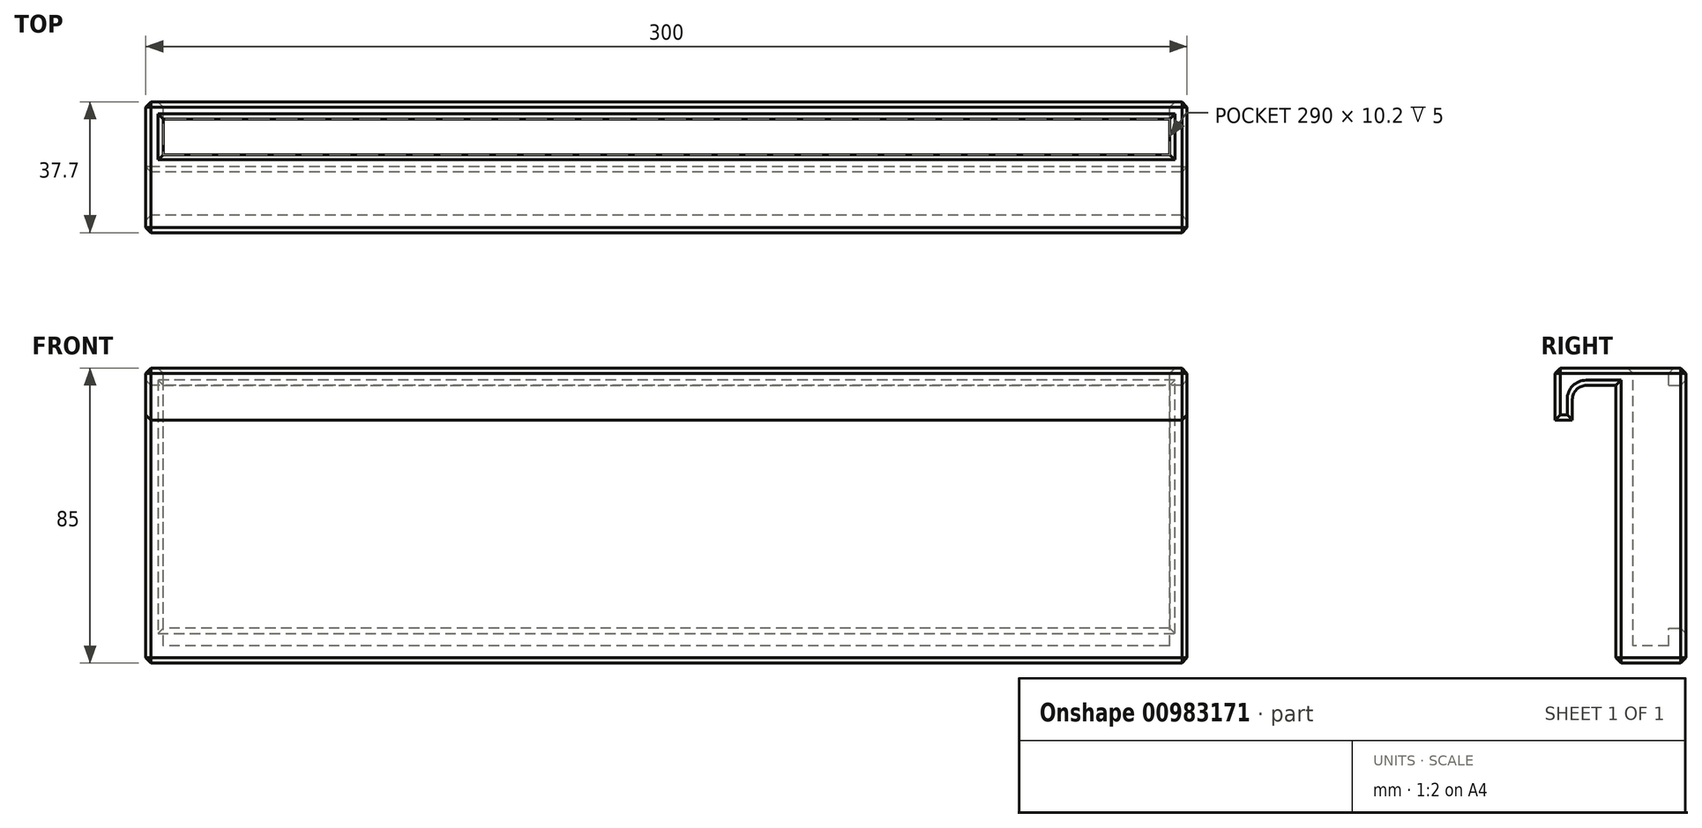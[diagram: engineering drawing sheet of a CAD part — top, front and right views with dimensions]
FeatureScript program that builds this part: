
annotation { "Feature Type Name" : "Feature", "Feature Type Description" : "" }
export const myFeature = defineFeature(function(context is Context, id is Id, definition is map)
    precondition{}
    {
        {
            var Q0;
            Q0=qCreatedBy(makeId("Right.planeOp"),FACE);
            var sketch = newSketch(context, id + "F0", { "sketchPlane" : qUnion([Q0])});
            skLineSegment(sketch, "E0.left", {"start": v(10.1, -42.5) * mm, "end": v(10.1, 42.5) * mm});
            skPoint(sketch, "E0.middle", {"position": v(0, 0) * mm});
            skLineSegment(sketch, "E1.top", {"start": v(5.1, -37.5) * mm, "end": v(-5.1, -37.5) * mm});
            skLineSegment(sketch, "E2.top", {"start": v(-10.1, 37.5) * mm, "end": v(-22.6, 37.5) * mm});
            skLineSegment(sketch, "E3.top", {"start": v(-22.6, 27.5) * mm, "end": v(-27.6, 27.5) * mm});
            skLineSegment(sketch, "E3.right", {"start": v(-27.6, 42.5) * mm, "end": v(-27.6, 27.5) * mm});
            skLineSegment(sketch, "E4.top", {"start": v(-5.1, 37.5) * mm, "end": v(5.1, 37.5) * mm});
            skLineSegment(sketch, "E5", {"start": v(5.1, -37.5) * mm, "end": v(5.1, 37.5) * mm});
            skLineSegment(sketch, "E6", {"start": v(-5.1, 37.5) * mm, "end": v(-5.1, -37.5) * mm});
            skLineSegment(sketch, "E7", {"start": v(-22.6, 37.5) * mm, "end": v(-22.6, 27.5) * mm});
            skLineSegment(sketch, "E8", {"start": v(-10.1, 37.5) * mm, "end": v(-10.1, -42.5) * mm});
            skLineSegment(sketch, "E9", {"start": v(-10.1, -42.5) * mm, "end": v(10.1, -42.5) * mm});
            skLineSegment(sketch, "E10", {"start": v(-27.6, 42.5) * mm, "end": v(10.1, 42.5) * mm});
            skLineSegment(sketch, "E11", {"start": v(0, 37.5) * mm, "end": v(0, -37.5) * mm, "construction": true});
            skLineSegment(sketch, "E12", {"start": v(-5.1, 0) * mm, "end": v(5.1, 0) * mm, "construction": true});
            skLineSegment(sketch, "E13", {"start": v(-16.35, 37.5) * mm, "end": v(-16.35, 20.18) * mm, "construction": true});
            skLineSegment(sketch, "E14", {"start": v(-22.6, 33.5) * mm, "end": v(-10.1, 33.5) * mm, "construction": true});
            skLineSegment(sketch, "E15", {"start": v(-18.6, 37.5) * mm, "end": v(-18.6, 19.62) * mm, "construction": true});
            skArc(sketch, "E16", {"start": v(-18.6, 37.5) * mm, "mid": v(-21.43, 36.33) * mm, "end": v(-22.6, 33.5) * mm});
            skLineSegment(sketch, "E17", {"start": v(-15.1, 37.5) * mm, "end": v(-15.1, 22.05) * mm, "construction": true});
            skLineSegment(sketch, "E18", {"start": v(-22.6, 32.5) * mm, "end": v(-10.1, 32.5) * mm, "construction": true});
            skArc(sketch, "E19", {"start": v(-15.1, 37.5) * mm, "mid": v(-11.56, 36.04) * mm, "end": v(-10.1, 32.5) * mm});
            skSolve(sketch);
        }
        {
            var Q0;
            Q0=makeQuery(id+"F0.imprint","IMPRINT",FACE,{"disambiguationData":[TD([[makeQuery(id+"F0.imprint","IMPRINT",EDGE,{"derivedFrom":sQuery(id+"F0.wireOp",EDGE,"E0.left")}),1.0]])]});
            var Q1;
            {var subQ3=sQuery(id+"F0.wireOp",EDGE,"7e27f287-87ae-4c6c-8f3d-3b3ba59f38b20.MirrorCS");Q1=makeQuery(id+"F0.imprint","IMPRINT",FACE,{"disambiguationData":[TD([[makeQuery(id+"F0.imprint","IMPRINT",EDGE,{"derivedFrom":subQ3}),1.0]])]});}
            var Q2;
            {var subQ3=sQuery(id+"F0.wireOp",EDGE,"E16");Q2=makeQuery(id+"F0.imprint","IMPRINT",FACE,{"disambiguationData":[TD([[makeQuery(id+"F0.imprint","IMPRINT",EDGE,{"derivedFrom":subQ3}),-1.0]])]});}
            var Q3;
            {var subQ3=sQuery(id+"F0.wireOp",EDGE,"E19");Q3=makeQuery(id+"F0.imprint","IMPRINT",FACE,{"disambiguationData":[TD([[makeQuery(id+"F0.imprint","IMPRINT",EDGE,{"derivedFrom":subQ3}),1.0]])]});}
            var Q4;
            Q4=makeQuery(id+"F0.imprint","IMPRINT",FACE,{"disambiguationData":[TD([[makeQuery(id+"F0.imprint","IMPRINT",EDGE,{"derivedFrom":sQuery(id+"F0.wireOp",EDGE,"E1.top")}),-1.0]])]});
            extrude(context, id + "F1", {"entities" : qUnion([Q0, Q1, Q2, Q3, Q4]), "depth" : 300 * mm, "offsetDistance" : 25 * mm});
        }
        {
            var Q0;
            Q0=makeQuery(id+"F1.opExtrude","SWEPT_FACE",FACE,{"disambiguationData":[OSD([sQuery(id+"F0.wireOp",EDGE,"E0.left")])]});
            var sketch = newSketch(context, id + "F2", { "sketchPlane" : qUnion([Q0])});
            skLineSegment(sketch, "E20.bottom", {"start": v(-295, 37.5) * mm, "end": v(-5, 37.5) * mm});
            skLineSegment(sketch, "E20.top", {"start": v(-295, -32.5) * mm, "end": v(-5, -32.5) * mm});
            skLineSegment(sketch, "E20.left", {"start": v(-295, 37.5) * mm, "end": v(-295, -32.5) * mm});
            skLineSegment(sketch, "E20.right", {"start": v(-5, 37.5) * mm, "end": v(-5, -32.5) * mm});
            skPoint(sketch, "E20.middle", {"position": v(-150, 0) * mm});
            skPoint(sketch, "E20.middle.positionSnap0", {"position": v(-150, 42.5) * mm});
            skPoint(sketch, "E20.centerSnap0", {"position": v(-150, 42.5) * mm});
            skSolve(sketch);
        }
        {
            var Q0;
            Q0=makeQuery(id+"F2.imprint","IMPRINT",FACE,{"disambiguationData":[TD([[makeQuery(id+"F2.imprint","IMPRINT",EDGE,{"derivedFrom":sQuery(id+"F2.wireOp",EDGE,"E20.bottom")}),-1.0]])]});
            extrude(context, id + "F3", {"entities" : qUnion([Q0]), "operationType" : NewBodyOperationType.REMOVE, "oppositeDirection" : true, "depth" : 5 * mm, "offsetDistance" : 25 * mm});
        }
        {
            var Q0;
            Q0=makeQuery(id+"F1.opExtrude","SWEPT_FACE",FACE,{"disambiguationData":[OSD([sQuery(id+"F0.wireOp",EDGE,"E10")])]});
            var sketch = newSketch(context, id + "F4", { "sketchPlane" : qUnion([Q0])});
            skLineSegment(sketch, "E21.bottom", {"start": v(295, 5.1) * mm, "end": v(5, 5.1) * mm});
            skLineSegment(sketch, "E21.top", {"start": v(295, -5.1) * mm, "end": v(5, -5.1) * mm});
            skLineSegment(sketch, "E21.left", {"start": v(295, 5.1) * mm, "end": v(295, -5.1) * mm});
            skLineSegment(sketch, "E21.right", {"start": v(5, 5.1) * mm, "end": v(5, -5.1) * mm});
            skSolve(sketch);
        }
        {
            var Q0;
            Q0=makeQuery(id+"F4.imprint","IMPRINT",FACE,{"disambiguationData":[TD([[makeQuery(id+"F4.imprint","IMPRINT",EDGE,{"derivedFrom":sQuery(id+"F4.wireOp",EDGE,"E21.bottom")}),1.0]])]});
            extrude(context, id + "F5", {"entities" : qUnion([Q0]), "operationType" : NewBodyOperationType.REMOVE, "oppositeDirection" : true, "depth" : 80 * mm, "offsetDistance" : 25 * mm});
        }
        {
            var Q0;
            Q0=makeQuery(id+"F1.opExtrude","CAP_FACE",FACE,{"disambiguationData":[OSD([sQuery(id+"F0.wireOp",EDGE,"E0.left"),sQuery(id+"F0.wireOp",EDGE,"E2.top"),sQuery(id+"F0.wireOp",EDGE,"E3.top"),sQuery(id+"F0.wireOp",EDGE,"E3.right"),sQuery(id+"F0.wireOp",EDGE,"E7"),sQuery(id+"F0.wireOp",EDGE,"E8"),sQuery(id+"F0.wireOp",EDGE,"E9"),sQuery(id+"F0.wireOp",EDGE,"E10"),sQuery(id+"F0.wireOp",EDGE,"E16"),sQuery(id+"F0.wireOp",EDGE,"E19")])],"isStart":false});
            var Q1;
            Q1=makeQuery(id+"F1.opExtrude","SWEPT_FACE",FACE,{"disambiguationData":[OSD([sQuery(id+"F0.wireOp",EDGE,"E0.left")])]});
            var Q2;
            Q2=makeQuery(id+"F1.opExtrude","SWEPT_FACE",FACE,{"disambiguationData":[OSD([sQuery(id+"F0.wireOp",EDGE,"E10")])]});
            var Q3;
            Q3=makeQuery(id+"F1.opExtrude","SWEPT_FACE",FACE,{"disambiguationData":[OSD([sQuery(id+"F0.wireOp",EDGE,"E9")])]});
            var Q4;
            Q4=makeQuery(id+"F1.opExtrude","CAP_FACE",FACE,{"disambiguationData":[OSD([sQuery(id+"F0.wireOp",EDGE,"E0.left"),sQuery(id+"F0.wireOp",EDGE,"E2.top"),sQuery(id+"F0.wireOp",EDGE,"E3.top"),sQuery(id+"F0.wireOp",EDGE,"E3.right"),sQuery(id+"F0.wireOp",EDGE,"E7"),sQuery(id+"F0.wireOp",EDGE,"E8"),sQuery(id+"F0.wireOp",EDGE,"E9"),sQuery(id+"F0.wireOp",EDGE,"E10"),sQuery(id+"F0.wireOp",EDGE,"E16"),sQuery(id+"F0.wireOp",EDGE,"E19")])],"isStart":true});
            chamfer(context, id + "F6", {"entities" : qUnion([Q0, Q1, Q2, Q3, Q4]), "width" : 1.5 * mm, "tangentPropagation" : true});
        }
    });
